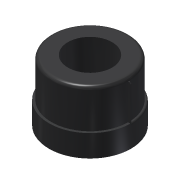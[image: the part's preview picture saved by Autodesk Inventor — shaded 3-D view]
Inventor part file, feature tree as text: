
AUTODESK INVENTOR PART (.ipt)
format: ipt  version: 2014 SP1 (Build 180222100, 222)  size: 147,968 bytes
history: native  units: in
note: dims shown in document units (in); Inventor stores cm internally (conversion verified against a paired STEP export)
features: extrude x4, sketch x4, chamfer x2, fillet x2
ambient origin geometry x8: Origin, YZ Plane, XZ Plane, XY Plane, X Axis, Y Axis, Z Axis, Center Point
bodies: Solid1 (feature_tree)
feature tree (12):
  extrude  "Extrusion1"  Depth=0.312in TaperAngle=0.0deg
  extrude  "Extrusion2"  Depth=0.55in TaperAngle=0.0deg
  extrude  "Extrusion3"  TaperAngle=180.0deg  [1 undecoded]
  chamfer  "Chamfer1"  Distance=0.5in
  chamfer  "Chamfer2"  Distance=0.02in Angle=45.0deg
  fillet  "Fillet1"  Radius=0.05in
  fillet  "Fillet2"  Radius=0.02in
  extrude  "Extrusion4"  Depth=0.02in
  sketch  "Sketch1"  dims[d0=1.16in d1=0.312in d2=0.0in]
  sketch  "Sketch2"  dims[d3=1.095in d4=0.55in d5=0.0in]
  sketch  "Sketch4"  dims[d7=180.0deg d8=180.0deg d9=0.5in d10=0.0in d11=0.02in d12=0.125in d13=45.0deg]
  sketch  "Sketch5"  dims[d14=0.02in d15=0.125in d16=45.0deg d17=0.05in d18=0.02in d19=0.625in d20=1.0in d21=0.0in]
note: 1 required parameter value undecoded (feature->parameter linkage not recoverable at this tier; creation-order binding heuristic only, values carry confidence <= 0.55)
